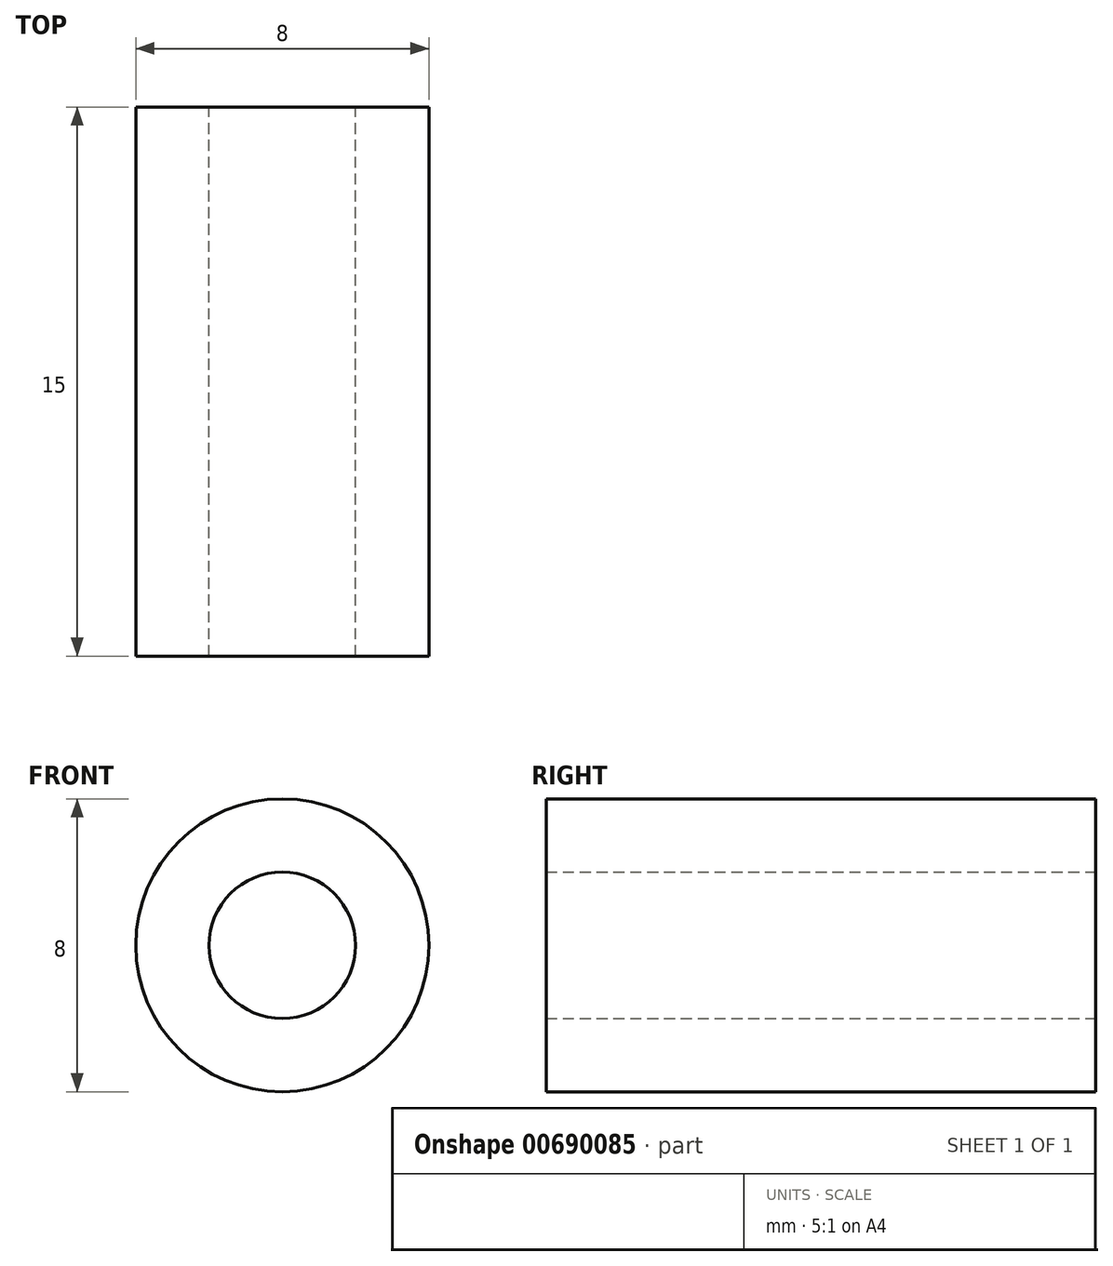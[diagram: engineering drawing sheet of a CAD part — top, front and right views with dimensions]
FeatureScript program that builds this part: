
annotation { "Feature Type Name" : "Feature", "Feature Type Description" : "" }
export const myFeature = defineFeature(function(context is Context, id is Id, definition is map)
    precondition{}
    {
        {
            var Q0;
            Q0=qCreatedBy(makeId("Front.planeOp"),FACE);
            var sketch = newSketch(context, id + "F0", { "sketchPlane" : qUnion([Q0])});
            skCircle(sketch, "E0", {"center": v(0, 0) * mm, "radius": 4 * mm});
            skCircle(sketch, "E1", {"center": v(0, 0) * mm, "radius": 2 * mm});
            skSolve(sketch);
        }
        {
            var Q0;
            Q0=makeQuery(id+"F0.imprint","IMPRINT",FACE,{"disambiguationData":[TD([[makeQuery(id+"F0.imprint","IMPRINT",EDGE,{"derivedFrom":sQuery(id+"F0.wireOp",EDGE,"E0")}),1.0]])]});
            extrude(context, id + "F1", {"entities" : qUnion([Q0]), "depth" : 15 * mm, "offsetDistance" : 25 * mm});
        }
    });
